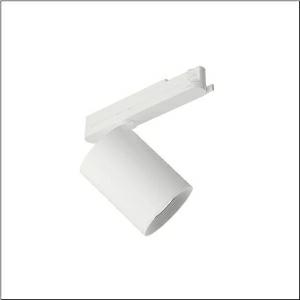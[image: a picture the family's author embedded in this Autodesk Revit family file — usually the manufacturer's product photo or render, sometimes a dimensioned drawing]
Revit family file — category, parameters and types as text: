
# Revit family: spot_21_51se14mbd5b
name_source: partatom
category: Lighting Fixtures
units: mm (PartAtom-declared; Revit-internal decimal feet)

## family parameters
Cut with Voids When Loaded = No
Host = Face
Light Source = No
Part Type = Normal
Room Calculation Point = No
Round Connector Dimension = Use Diameter
Shared = No

## types (1)
- --- (1 x LED, 5490 lm, 41.5 W, 4000K)
    Apparent Load = 42 VA
    CIE Flux Codes = 96 99 100 100 100
    Color Rendering = 90
    Color Temperature = 4000K
    Default Elevation = 1800 mm
    Description = Spot 21, directional spotlight, light control with lens, of PMMA, LED rated luminous flux: 5.270lm, light colour: 940, control gear: ECG Multilumen, with 3-phase adapter, mains connection: 220..240V, AC, 50/60Hz, of aluminium, traffic white (RAL 9016), length: 213mm, diameter: 105mm, protection rating (complete): IP20, insulation class (complete): insulation class I (protective earthing), certification: CE, impact resistance: IK02, permissible ambient temperature for indoor applications: -20..+40°C, packaging unit: 1 piece
    Height = 175 mm
    Lamp = 1 x LED
    Lamp Light Flux = 5490 lm
    Lamp Power = 41.5 W
    Lamp count = 1
    Length = 105 mm
    Luminous efficacy = 132 lm/W
    Manufacturer = Siteco
    ModVariant = No
    Model = 51SE14MBD5B
    Mounting Place = Ceiling
    Mounting Type = Pendant
    Number of Poles = 1
    OnlyDefault = Yes
    Power Factor = 1
    Product Name = Spot 21
    Product group = directional spotlight
    ProductGroupID = 906
    Protection Class = Protection class I
    Protection Degree = IP 20
    RLX_Detail_Level = 1
    RLX_Emergency_Light_Flux = 0 lm
    RLX_Emergency_Type = 0
    RLX_Emergency_Type_DB = No
    RlxData = <blob elided: 17605 chars, md5=3bab5055>
    Socket = socket
    Standby Power = 0 W
    System Light Flux = 5490 lm
    System Power = 42 W
    Type Comments = factory setting: luminous flux: 100 % | (ON | ON | ON | ON) | 1050 mA
    Type Image = l_1003976.jpg
    URL = http://relux.com
    VarID = @adj_143610
    Voltage = 0 V
    Weight = 0.00 kg
    Width = 0 mm  [stored 0 ft]

note: [stored X ft] marks values corroborated as IEEE doubles in the binary element streams (Revit-internal decimal feet)

## geometry (parser evidence)
native form markers: Blend x4, Sweep x11
no freeform markers — native parametric forms only
